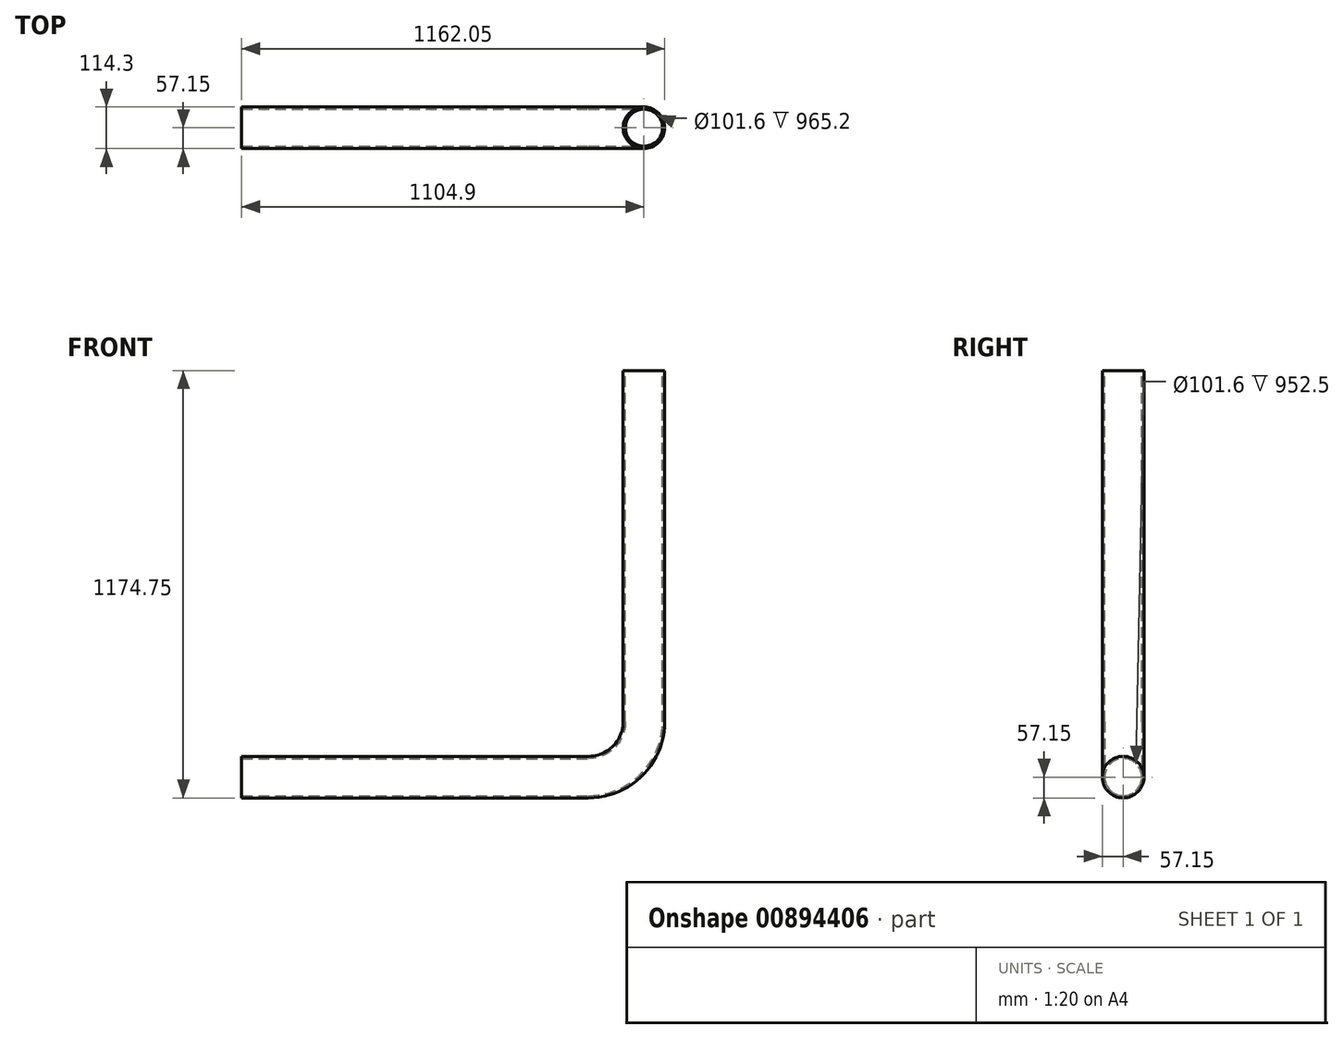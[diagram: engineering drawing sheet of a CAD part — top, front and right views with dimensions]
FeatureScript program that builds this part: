
annotation { "Feature Type Name" : "Feature", "Feature Type Description" : "" }
export const myFeature = defineFeature(function(context is Context, id is Id, definition is map)
    precondition{}
    {
        {
            var Q0;
            Q0=qCreatedBy(makeId("Front.planeOp"),FACE);
            var sketch = newSketch(context, id + "F0", { "sketchPlane" : qUnion([Q0])});
            skLineSegment(sketch, "E0", {"start": v(0, 0) * mm, "end": v(152.4, 0) * mm});
            skLineSegment(sketch, "E1", {"start": v(304.8, 152.4) * mm, "end": v(304.8, 304.8) * mm});
            skPoint(sketch, "E2", {"position": v(152.4, 0) * mm});
            skPoint(sketch, "E3", {"position": v(304.8, 152.4) * mm});
            skArc(sketch, "E4", {"start": v(152.4, 0) * mm, "mid": v(260.16, 44.64) * mm, "end": v(304.8, 152.4) * mm});
            skPoint(sketch, "E5.orphan", {"position": v(304.8, 0) * mm});
            skSolve(sketch);
        }
        {
            var Q0;
            Q0=qCreatedBy(makeId("Right.planeOp"),FACE);
            var sketch = newSketch(context, id + "F1", { "sketchPlane" : qUnion([Q0])});
            skCircle(sketch, "E6", {"center": v(0, 0) * mm, "radius": 57.15 * mm});
            skCircle(sketch, "E7", {"center": v(0, 0) * mm, "radius": 50.8 * mm});
            skSolve(sketch);
        }
        {
            var Q0;
            Q0=makeQuery(id+"F1.imprint","IMPRINT",FACE,{"disambiguationData":[TD([[makeQuery(id+"F1.imprint","IMPRINT",EDGE,{"derivedFrom":sQuery(id+"F1.wireOp",EDGE,"E6")}),1.0]])]});
            var Q1;
            Q1=sQuery(id+"F0.wireOp",EDGE,"E0");
            var Q2;
            Q2=sQuery(id+"F0.wireOp",EDGE,"E4");
            var Q3;
            Q3=sQuery(id+"F0.wireOp",EDGE,"E1");
            sweep(context, id + "F2", {"profiles" : qUnion([Q0]), "path" : qUnion([Q1, Q2, Q3])});
        }
        {
            var Q0;
            Q0=makeQuery(id+"F2.opSweep","CAP_FACE",FACE,{"disambiguationData":[OSD([sQuery(id+"F0.wireOp",VERTEX,"E1.end"),sQuery(id+"F1.wireOp",EDGE,"E6"),sQuery(id+"F1.wireOp",EDGE,"E7")])],"isStart":false});
            extrude(context, id + "F3", {"entities" : qUnion([Q0]), "operationType" : NewBodyOperationType.ADD, "depth" : 812.8 * mm, "offsetDistance" : 25.4 * mm});
        }
        {
            var Q0;
            Q0=makeQuery(id+"F2.opSweep","CAP_FACE",FACE,{"disambiguationData":[OSD([sQuery(id+"F0.wireOp",VERTEX,"E0.start"),sQuery(id+"F1.wireOp",EDGE,"E6"),sQuery(id+"F1.wireOp",EDGE,"E7")])],"isStart":true});
            extrude(context, id + "F4", {"entities" : qUnion([Q0]), "operationType" : NewBodyOperationType.ADD, "depth" : 800.1 * mm, "offsetDistance" : 25.4 * mm});
        }
    });
